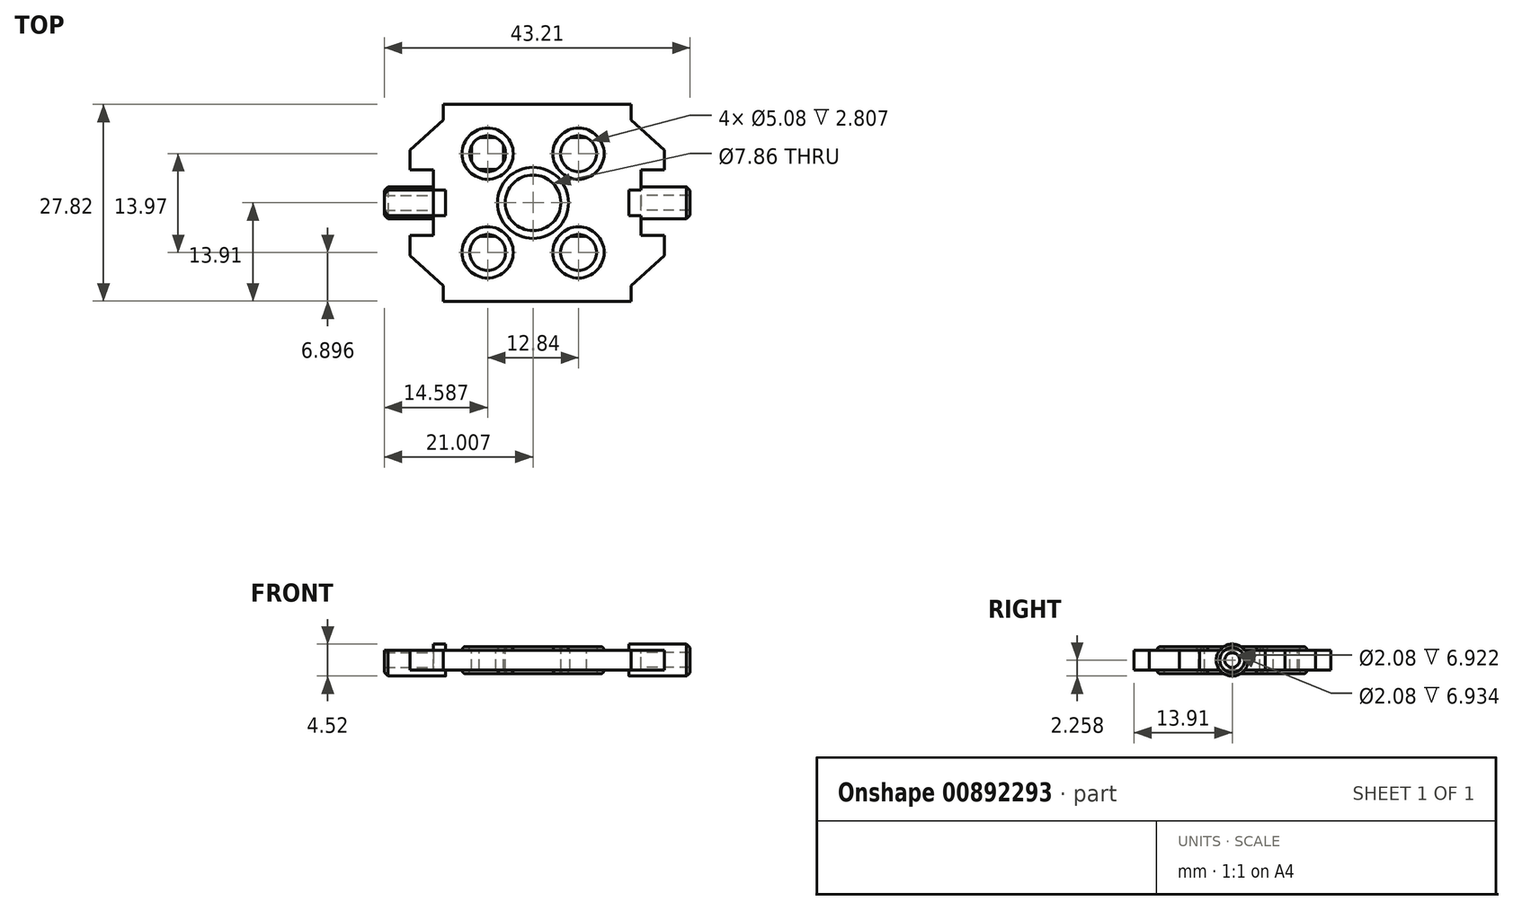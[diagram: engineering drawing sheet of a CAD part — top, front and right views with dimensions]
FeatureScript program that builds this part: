
annotation { "Feature Type Name" : "Feature", "Feature Type Description" : "" }
export const myFeature = defineFeature(function(context is Context, id is Id, definition is map)
    precondition{}
    {
        {
            var Q0;
            Q0=qCreatedBy(makeId("Top.planeOp"),FACE);
            var sketch = newSketch(context, id + "F0", { "sketchPlane" : qUnion([Q0])});
            skLineSegment(sketch, "E0.bottom", {"start": v(-17.98, 13.91) * mm, "end": v(17.98, 13.91) * mm});
            skLineSegment(sketch, "E0.top", {"start": v(-17.98, -13.91) * mm, "end": v(17.98, -13.91) * mm});
            skLineSegment(sketch, "E0.left", {"start": v(-17.98, 13.91) * mm, "end": v(-17.98, -13.91) * mm});
            skLineSegment(sketch, "E0.right", {"start": v(17.98, 13.91) * mm, "end": v(17.98, -13.91) * mm});
            skLineSegment(sketch, "E1", {"start": v(17.98, 0) * mm, "end": v(-17.98, 0) * mm});
            skSolve(sketch);
        }
        {
            var Q0;
            Q0=qSketchRegion(id+"F0",true);
            extrude(context, id + "F1", {"entities" : qUnion([Q0]), "depth" : 2.76 * mm, "offsetDistance" : 25.4 * mm});
        }
        {
            var Q0;
            Q0=makeQuery(id+"F1.opExtrude","CAP_FACE",FACE,{"disambiguationData":[OSD([sQuery(id+"F0.wireOp",EDGE,"E0.bottom"),sQuery(id+"F0.wireOp",EDGE,"E0.top"),sQuery(id+"F0.wireOp",EDGE,"E0.left"),sQuery(id+"F0.wireOp",EDGE,"E0.right")])],"isStart":false});
            var sketch = newSketch(context, id + "F2", { "sketchPlane" : qUnion([Q0])});
            skPoint(sketch, "E2", {"position": v(26.78, 13.91) * mm});
            skLineSegment(sketch, "E3", {"start": v(17.98, 0) * mm, "end": v(17.98, 3.7) * mm});
            skLineSegment(sketch, "E4", {"start": v(17.98, 3.7) * mm, "end": v(17.98, 6.51) * mm});
            skLineSegment(sketch, "E5", {"start": v(17.98, -5.58) * mm, "end": v(17.98, -8.4) * mm});
            skPoint(sketch, "E6", {"position": v(26.78, -13.91) * mm});
            skPoint(sketch, "E7", {"position": v(-13.25, -13.91) * mm});
            skPoint(sketch, "E8", {"position": v(-13.25, 13.91) * mm});
            skLineSegment(sketch, "E9", {"start": v(-14.67, 0) * mm, "end": v(-14.67, 4.64) * mm});
            skLineSegment(sketch, "E10", {"start": v(-14.67, 0) * mm, "end": v(-14.67, -4.64) * mm});
            skLineSegment(sketch, "E11", {"start": v(-14.67, -4.64) * mm, "end": v(-17.98, -4.64) * mm});
            skLineSegment(sketch, "E12", {"start": v(-14.67, 4.64) * mm, "end": v(-17.98, 4.64) * mm});
            skLineSegment(sketch, "E13", {"start": v(-13.25, 13.91) * mm, "end": v(-13.25, 11.74) * mm});
            skLineSegment(sketch, "E14", {"start": v(-13.25, -13.91) * mm, "end": v(-13.25, -11.74) * mm});
            skLineSegment(sketch, "E15", {"start": v(-17.98, -4.64) * mm, "end": v(-17.98, -7.45) * mm});
            skLineSegment(sketch, "E16", {"start": v(-17.98, 4.64) * mm, "end": v(-17.98, 7.45) * mm});
            skLineSegment(sketch, "E17", {"start": v(-17.98, 7.45) * mm, "end": v(-13.25, 11.74) * mm});
            skLineSegment(sketch, "E18", {"start": v(-13.25, -11.74) * mm, "end": v(-17.98, -7.45) * mm});
            skCircle(sketch, "E19", {"center": v(-0.6, 0) * mm, "radius": 3.93 * mm});
            skLineSegment(sketch, "E20", {"start": v(17.98, 6.96) * mm, "end": v(-32.7, 6.96) * mm, "construction": true});
            skLineSegment(sketch, "E21", {"start": v(17.98, 0) * mm, "end": v(17.98, 13.91) * mm, "construction": true});
            skPoint(sketch, "E22", {"position": v(-7.01, 6.96) * mm});
            skPoint(sketch, "E23", {"position": v(5.83, 6.96) * mm});
            skPoint(sketch, "E24", {"position": v(18.67, 6.96) * mm});
            skPoint(sketch, "E25", {"position": v(31.5, 6.96) * mm});
            skPoint(sketch, "E26", {"position": v(-19.85, 6.96) * mm});
            skLineSegment(sketch, "E27", {"start": v(-7.01, 6.96) * mm, "end": v(-7.01, -13.91) * mm, "construction": true});
            skLineSegment(sketch, "E28", {"start": v(5.83, 6.96) * mm, "end": v(5.83, -13.91) * mm, "construction": true});
            skLineSegment(sketch, "E29", {"start": v(17.98, 0) * mm, "end": v(17.98, -13.91) * mm, "construction": true});
            skPoint(sketch, "E30", {"position": v(17.98, -6.96) * mm});
            skLineSegment(sketch, "E31", {"start": v(17.98, -6.96) * mm, "end": v(-17.98, -6.96) * mm, "construction": true});
            skCircle(sketch, "E32", {"center": v(-7.01, 6.96) * mm, "radius": 2.54 * mm});
            skPoint(sketch, "E33", {"position": v(5.83, 0) * mm});
            skPoint(sketch, "E34", {"position": v(18.67, 0) * mm});
            skPoint(sketch, "E35", {"position": v(-7.01, 0) * mm});
            skPoint(sketch, "E36", {"position": v(-19.85, 0) * mm});
            skLineSegment(sketch, "E37", {"start": v(18.67, 0) * mm, "end": v(5.83, 0) * mm});
            skLineSegment(sketch, "E38", {"start": v(-19.85, 0) * mm, "end": v(-7.01, 0) * mm});
            skLineSegment(sketch, "E39.left", {"start": v(16.42, -9.2) * mm, "end": v(16.42, -4.7) * mm});
            skPoint(sketch, "E39.middle", {"position": v(19.26, -6.96) * mm});
            skLineSegment(sketch, "E40.2.1.0", {"start": v(-9.26, 4.7) * mm, "end": v(-4.76, 4.7) * mm});
            skLineSegment(sketch, "E40.2.1.1", {"start": v(-9.26, 4.7) * mm, "end": v(-9.26, 9.2) * mm});
            skLineSegment(sketch, "E40.2.1.2", {"start": v(-9.26, 9.2) * mm, "end": v(-4.76, 9.2) * mm});
            skLineSegment(sketch, "E40.2.1.3", {"start": v(-4.76, 4.7) * mm, "end": v(-4.76, 9.2) * mm});
            skLineSegment(sketch, "E41.bottom", {"start": v(-17.98, 13.91) * mm, "end": v(17.98, 13.91) * mm});
            skLineSegment(sketch, "E41.top", {"start": v(-17.98, -13.91) * mm, "end": v(17.98, -13.91) * mm});
            skLineSegment(sketch, "E41.left", {"start": v(-17.98, 13.91) * mm, "end": v(-17.98, -13.91) * mm});
            skLineSegment(sketch, "E41.right", {"start": v(17.98, 13.91) * mm, "end": v(17.98, -13.91) * mm});
            skPoint(sketch, "E42", {"position": v(0, 13.91) * mm});
            skLineSegment(sketch, "E43", {"start": v(17.98, 13.91) * mm, "end": v(-17.98, 13.91) * mm});
            skLineSegment(sketch, "E44", {"start": v(13.25, 13.91) * mm, "end": v(13.25, 11.74) * mm});
            skLineSegment(sketch, "E45", {"start": v(13.25, 11.74) * mm, "end": v(17.98, 7.45) * mm});
            skLineSegment(sketch, "E46", {"start": v(17.98, 7.45) * mm, "end": v(17.98, 4.64) * mm});
            skLineSegment(sketch, "E47", {"start": v(17.98, 4.64) * mm, "end": v(14.67, 4.64) * mm});
            skLineSegment(sketch, "E48", {"start": v(14.67, 4.64) * mm, "end": v(14.67, -4.64) * mm});
            skLineSegment(sketch, "E49", {"start": v(14.67, -4.64) * mm, "end": v(17.98, -4.64) * mm});
            skLineSegment(sketch, "E50", {"start": v(17.98, -4.64) * mm, "end": v(17.98, -7.45) * mm});
            skLineSegment(sketch, "E51", {"start": v(17.98, -7.45) * mm, "end": v(13.25, -11.74) * mm});
            skLineSegment(sketch, "E52", {"start": v(13.25, -11.74) * mm, "end": v(13.25, -13.91) * mm});
            skPoint(sketch, "E53", {"position": v(14.67, 0) * mm});
            skPoint(sketch, "E54", {"position": v(-4.76, 6.96) * mm});
            skPoint(sketch, "E55", {"position": v(7.94, 6.96) * mm});
            skPoint(sketch, "E55.positionSnap0", {"position": v(8.07, 6.96) * mm});
            skPoint(sketch, "E56", {"position": v(-4.76, -6.96) * mm});
            skPoint(sketch, "E57", {"position": v(8.07, -6.96) * mm});
            skCircle(sketch, "E58.0.1.0", {"center": v(-7.01, -7.01) * mm, "radius": 2.54 * mm});
            skLineSegment(sketch, "E58.0.1.1", {"start": v(-9.26, -4.77) * mm, "end": v(-4.76, -4.77) * mm});
            skLineSegment(sketch, "E58.0.1.2", {"start": v(-4.76, -9.26) * mm, "end": v(-4.76, -4.77) * mm});
            skLineSegment(sketch, "E58.0.1.3", {"start": v(-9.26, -9.26) * mm, "end": v(-4.76, -9.26) * mm});
            skLineSegment(sketch, "E58.0.1.4", {"start": v(-9.26, -9.26) * mm, "end": v(-9.26, -4.77) * mm});
            skCircle(sketch, "E58.1.0.0", {"center": v(5.83, 6.96) * mm, "radius": 2.54 * mm});
            skLineSegment(sketch, "E58.1.0.1", {"start": v(3.58, 9.2) * mm, "end": v(8.07, 9.2) * mm});
            skLineSegment(sketch, "E58.1.0.2", {"start": v(8.07, 4.7) * mm, "end": v(8.07, 9.2) * mm});
            skLineSegment(sketch, "E58.1.0.3", {"start": v(3.58, 4.7) * mm, "end": v(8.07, 4.7) * mm});
            skLineSegment(sketch, "E58.1.0.4", {"start": v(3.58, 4.7) * mm, "end": v(3.58, 9.2) * mm});
            skCircle(sketch, "E58.1.1.0", {"center": v(5.83, -7.01) * mm, "radius": 2.54 * mm});
            skLineSegment(sketch, "E58.1.1.1", {"start": v(3.58, -4.77) * mm, "end": v(8.07, -4.77) * mm});
            skLineSegment(sketch, "E58.1.1.2", {"start": v(8.07, -9.26) * mm, "end": v(8.07, -4.77) * mm});
            skLineSegment(sketch, "E58.1.1.3", {"start": v(3.58, -9.26) * mm, "end": v(8.07, -9.26) * mm});
            skLineSegment(sketch, "E58.1.1.4", {"start": v(3.58, -9.26) * mm, "end": v(3.58, -4.77) * mm});
            skLineSegment(sketch, "E58.direction1", {"start": v(-7.01, 6.96) * mm, "end": v(5.83, 6.96) * mm, "construction": true});
            skLineSegment(sketch, "E58.direction2", {"start": v(-7.01, 6.96) * mm, "end": v(-7.01, -7.01) * mm, "construction": true});
            skLineSegment(sketch, "E59", {"start": v(5.83, 0) * mm, "end": v(-0.6, 0) * mm});
            skLineSegment(sketch, "E60", {"start": v(-7.01, 0) * mm, "end": v(-0.6, 0) * mm});
            skSolve(sketch);
        }
        {
            var Q0;
            Q0=makeQuery(id+"F2.imprint","IMPRINT",FACE,{"disambiguationData":[TD([[makeQuery(id+"F2.imprint","IMPRINT",EDGE,{"derivedFrom":sQuery(id+"F2.wireOp",EDGE,"zKyvtmt8-tCjY-tQvq-sh6t-lBbuTK4CHgfQ")}),1.0]])]});
            var Q1;
            {var subQ0=sQuery(id+"F2.wireOp",EDGE,"nGXZYah3-xuGq-2yHy-m2No-0d3Pi9Qq722P");Q1=makeQuery(id+"F2.imprint","IMPRINT",FACE,{"disambiguationData":[TD([[makeQuery(id+"F2.imprint","IMPRINT",EDGE,{"derivedFrom":subQ0}),1.0]])]});}
            var Q2;
            {var subQ0=sQuery(id+"F2.wireOp",EDGE,"yPbE09O0-nCyG-tVRH-j9K3-g5R8uc3CmmFN");Q2=makeQuery(id+"F2.imprint","IMPRINT",FACE,{"disambiguationData":[TD([[makeQuery(id+"F2.imprint","IMPRINT",EDGE,{"derivedFrom":subQ0}),-1.0]])]});}
            var Q3;
            {var subQ0=sQuery(id+"F2.wireOp",EDGE,"E14");Q3=makeQuery(id+"F2.imprint","IMPRINT",FACE,{"disambiguationData":[TD([[makeQuery(id+"F2.imprint","IMPRINT",EDGE,{"derivedFrom":subQ0}),1.0]])]});}
            var Q4;
            Q4=makeQuery(id+"F2.imprint","IMPRINT",FACE,{"disambiguationData":[TD([[makeQuery(id+"F2.imprint","IMPRINT",EDGE,{"derivedFrom":sQuery(id+"F2.wireOp",EDGE,"E9")}),1.0]])]});
            var Q5;
            {var subQ0=sQuery(id+"F2.wireOp",EDGE,"E13");Q5=makeQuery(id+"F2.imprint","IMPRINT",FACE,{"disambiguationData":[TD([[makeQuery(id+"F2.imprint","IMPRINT",EDGE,{"derivedFrom":subQ0}),-1.0]])]});}
            extrude(context, id + "F3", {"entities" : qUnion([Q0, Q1, Q2, Q3, Q4, Q5]), "operationType" : NewBodyOperationType.REMOVE, "oppositeDirection" : true, "depth" : 25.4 * mm, "offsetDistance" : 25.4 * mm});
        }
        {
            var Q0;
            Q0=makeQuery(id+"F2.imprint","IMPRINT",FACE,{"disambiguationData":[TD([[makeQuery(id+"F2.imprint","IMPRINT",EDGE,{"derivedFrom":sQuery(id+"F2.wireOp",EDGE,"fuK7n6Y2-Enzt-2XlE-SA73-k2Jc5K4om95h")}),1.0]])]});
            var Q1;
            {var subQ0=sQuery(id+"F2.wireOp",EDGE,"sv07lWKE-gPZX-1UWt-FJWq-DTTsMFg5NSMi");var subQ1=sQuery(id+"F2.wireOp",EDGE,"E38");var subQ2=makeQuery(id+"F2.imprint","INTERSECT",VERTEX,{"disambiguationData":[OD(0.0)],"derivedFrom":[subQ1,subQ0]});Q1=makeQuery(id+"F2.imprint","IMPRINT",FACE,{"disambiguationData":[TD([[makeQuery(id+"F2.imprint","IMPRINT",EDGE,{"disambiguationData":[TD([[subQ2,-1.0]])],"derivedFrom":subQ1}),-1.0]])]});}
            var Q2;
            {var subQ0=sQuery(id+"F2.wireOp",EDGE,"sv07lWKE-gPZX-1UWt-FJWq-DTTsMFg5NSMi");var subQ1=sQuery(id+"F2.wireOp",EDGE,"E38");var subQ2=makeQuery(id+"F2.imprint","INTERSECT",VERTEX,{"disambiguationData":[OD(0.0)],"derivedFrom":[subQ1,subQ0]});Q2=makeQuery(id+"F2.imprint","IMPRINT",FACE,{"disambiguationData":[TD([[makeQuery(id+"F2.imprint","IMPRINT",EDGE,{"disambiguationData":[TD([[subQ2,-1.0]])],"derivedFrom":subQ1}),1.0]])]});}
            var Q3;
            Q3=makeQuery(id+"F2.imprint","IMPRINT",FACE,{"disambiguationData":[TD([[makeQuery(id+"F2.imprint","IMPRINT",EDGE,{"derivedFrom":sQuery(id+"F2.wireOp",EDGE,"E19")}),1.0]])]});
            var Q4;
            {var subQ0=sQuery(id+"F2.wireOp",EDGE,"gV5skUVd-Vbjl-6Grx-gXeV-zpvUfDL4PLVQ");var subQ1=sQuery(id+"F2.wireOp",EDGE,"E37");var subQ2=makeQuery(id+"F2.imprint","INTERSECT",VERTEX,{"disambiguationData":[OD(0.0)],"derivedFrom":[subQ1,subQ0]});Q4=makeQuery(id+"F2.imprint","IMPRINT",FACE,{"disambiguationData":[TD([[makeQuery(id+"F2.imprint","IMPRINT",EDGE,{"disambiguationData":[TD([[subQ2,1.0]])],"derivedFrom":subQ1}),1.0]])]});}
            var Q5;
            {var subQ0=sQuery(id+"F2.wireOp",EDGE,"gV5skUVd-Vbjl-6Grx-gXeV-zpvUfDL4PLVQ");var subQ1=sQuery(id+"F2.wireOp",EDGE,"E37");var subQ2=makeQuery(id+"F2.imprint","INTERSECT",VERTEX,{"disambiguationData":[OD(0.0)],"derivedFrom":[subQ1,subQ0]});Q5=makeQuery(id+"F2.imprint","IMPRINT",FACE,{"disambiguationData":[TD([[makeQuery(id+"F2.imprint","IMPRINT",EDGE,{"disambiguationData":[TD([[subQ2,1.0]])],"derivedFrom":subQ1}),-1.0]])]});}
            var Q6;
            Q6=makeQuery(id+"F2.imprint","IMPRINT",FACE,{"disambiguationData":[TD([[makeQuery(id+"F2.imprint","IMPRINT",EDGE,{"derivedFrom":sQuery(id+"F2.wireOp",EDGE,"omkNjfGR-ckuW-d5aa-qWtX-TfsBPBlHMN8u")}),1.0]])]});
            var Q7;
            Q7=makeQuery(id+"F2.imprint","IMPRINT",FACE,{"disambiguationData":[TD([[makeQuery(id+"F2.imprint","IMPRINT",EDGE,{"derivedFrom":sQuery(id+"F2.wireOp",EDGE,"E32")}),1.0]])]});
            var Q8;
            Q8=makeQuery(id+"F2.imprint","IMPRINT",FACE,{"disambiguationData":[TD([[makeQuery(id+"F2.imprint","IMPRINT",EDGE,{"derivedFrom":sQuery(id+"F2.wireOp",EDGE,"wbXKtzry-o3Vx-0E5J-MFbw-KvrlOybN9rRN")}),1.0]])]});
            var Q9;
            Q9=makeQuery(id+"F2.imprint","IMPRINT",FACE,{"disambiguationData":[TD([[makeQuery(id+"F2.imprint","IMPRINT",EDGE,{"derivedFrom":sQuery(id+"F2.wireOp",EDGE,"Ppe3M46U-QorI-ucGU-aqDp-dvkcDBRh25Wz")}),1.0]])]});
            var Q10;
            Q10=makeQuery(id+"F2.imprint","IMPRINT",FACE,{"disambiguationData":[TD([[makeQuery(id+"F2.imprint","IMPRINT",EDGE,{"derivedFrom":sQuery(id+"F2.wireOp",EDGE,"4vAETKog-jQpa-BSM7-OqoW-5IxsvznHgaLA")}),1.0]])]});
            var Q11;
            Q11=makeQuery(id+"F2.imprint","IMPRINT",FACE,{"disambiguationData":[TD([[makeQuery(id+"F2.imprint","IMPRINT",EDGE,{"derivedFrom":sQuery(id+"F2.wireOp",EDGE,"5XKSeXba-nxxC-YXAP-KxCt-XMvB8Zbv8VPG")}),1.0]])]});
            var Q12;
            Q12=makeQuery(id+"F2.imprint","IMPRINT",FACE,{"disambiguationData":[TD([[makeQuery(id+"F2.imprint","IMPRINT",EDGE,{"derivedFrom":sQuery(id+"F2.wireOp",EDGE,"9KXrDHUh-3l1R-qzUI-8NNp-dQZea570rMoK")}),1.0]])]});
            var Q13;
            {var subQ4=sQuery(id+"F2.wireOp",EDGE,"E44");Q13=makeQuery(id+"F2.imprint","IMPRINT",FACE,{"disambiguationData":[TD([[makeQuery(id+"F2.imprint","IMPRINT",EDGE,{"derivedFrom":subQ4}),1.0]])]});}
            var Q14;
            {var subQ0=sQuery(id+"F2.wireOp",EDGE,"E52");Q14=makeQuery(id+"F2.imprint","IMPRINT",FACE,{"disambiguationData":[TD([[makeQuery(id+"F2.imprint","IMPRINT",EDGE,{"derivedFrom":subQ0}),1.0]])]});}
            var Q15;
            {var subQ1=sQuery(id+"F2.wireOp",EDGE,"E58.1.0.0");var subQ8=sQuery(id+"F2.wireOp",EDGE,"E58.1.0.1");var subQ11=makeQuery(id+"F2.imprint","INTERSECT",VERTEX,{"disambiguationData":[OD(0.0)],"derivedFrom":[subQ1,subQ8]});Q15=makeQuery(id+"F2.imprint","IMPRINT",FACE,{"disambiguationData":[TD([[makeQuery(id+"F2.imprint","IMPRINT",EDGE,{"disambiguationData":[TD([[subQ11,1.0]])],"derivedFrom":subQ1}),1.0]])]});}
            var Q16;
            {var subQ1=sQuery(id+"F2.wireOp",EDGE,"E58.1.1.0");var subQ8=sQuery(id+"F2.wireOp",EDGE,"E58.1.1.1");var subQ11=makeQuery(id+"F2.imprint","INTERSECT",VERTEX,{"disambiguationData":[OD(0.0)],"derivedFrom":[subQ1,subQ8]});Q16=makeQuery(id+"F2.imprint","IMPRINT",FACE,{"disambiguationData":[TD([[makeQuery(id+"F2.imprint","IMPRINT",EDGE,{"disambiguationData":[TD([[subQ11,1.0]])],"derivedFrom":subQ1}),1.0]])]});}
            var Q17;
            {var subQ1=sQuery(id+"F2.wireOp",EDGE,"E58.0.1.0");var subQ8=sQuery(id+"F2.wireOp",EDGE,"E58.0.1.1");var subQ11=makeQuery(id+"F2.imprint","INTERSECT",VERTEX,{"disambiguationData":[OD(0.0)],"derivedFrom":[subQ1,subQ8]});Q17=makeQuery(id+"F2.imprint","IMPRINT",FACE,{"disambiguationData":[TD([[makeQuery(id+"F2.imprint","IMPRINT",EDGE,{"disambiguationData":[TD([[subQ11,1.0]])],"derivedFrom":subQ1}),1.0]])]});}
            extrude(context, id + "F4", {"entities" : qUnion([Q0, Q1, Q2, Q3, Q4, Q5, Q6, Q7, Q8, Q9, Q10, Q11, Q12, Q13, Q14, Q15, Q16, Q17]), "operationType" : NewBodyOperationType.REMOVE, "oppositeDirection" : true, "depth" : 25.4 * mm, "offsetDistance" : 25.4 * mm});
        }
        {
            var Q0;
            Q0=makeQuery(id+"F3.boolean.opBoolean","COPY",FACE,{"derivedFrom":makeQuery(id+"F3.opExtrude","SWEPT_FACE",FACE,{"disambiguationData":[OSD([sQuery(id+"F2.wireOp",EDGE,"E9"),sQuery(id+"F2.wireOp",EDGE,"E10")])]})});
            var sketch = newSketch(context, id + "F5", { "sketchPlane" : qUnion([Q0])});
            skLineSegment(sketch, "E61", {"start": v(0, 0) * mm, "end": v(0, 2.76) * mm, "construction": true});
            skCircle(sketch, "E62", {"center": v(0, 1.38) * mm, "radius": 2.26 * mm});
            skCircle(sketch, "E63", {"center": v(0, 1.38) * mm, "radius": 1.04 * mm});
            skSolve(sketch);
        }
        {
            var Q0;
            Q0=makeQuery(id+"F5.imprint","IMPRINT",FACE,{"disambiguationData":[TD([[makeQuery(id+"F5.imprint","IMPRINT",EDGE,{"derivedFrom":sQuery(id+"F5.wireOp",EDGE,"E63")}),-1.0]])]});
            var Q1;
            {var subQ0=sQuery(id+"F5.wireOp",EDGE,"E62");var subQ1=makeQuery(id+"F3.boolean.opBoolean","COPY",EDGE,{"derivedFrom":makeQuery(id+"F3.opExtrude","CAP_EDGE",EDGE,{"disambiguationData":[OSD([sQuery(id+"F2.wireOp",EDGE,"E9"),sQuery(id+"F2.wireOp",EDGE,"E10")])],"isStart":true})});var subQ2=makeQuery(id+"F5.imprint","INTERSECT",VERTEX,{"disambiguationData":[OD(0.0)],"derivedFrom":[subQ1,subQ0]});Q1=makeQuery(id+"F5.imprint","IMPRINT",FACE,{"disambiguationData":[TD([[makeQuery(id+"F5.imprint","IMPRINT",EDGE,{"disambiguationData":[TD([[subQ2,1.0]])],"derivedFrom":subQ0}),1.0]])]});}
            var Q2;
            {var subQ0=sQuery(id+"F5.wireOp",EDGE,"E62");var subQ1=makeQuery(id+"F3.boolean.opBoolean","INTERSECT",EDGE,{"derivedFrom":[makeQuery(id+"F1.opExtrude","CAP_FACE",FACE,{"disambiguationData":[OSD([sQuery(id+"F0.wireOp",EDGE,"E0.bottom"),sQuery(id+"F0.wireOp",EDGE,"E0.top"),sQuery(id+"F0.wireOp",EDGE,"E0.left"),sQuery(id+"F0.wireOp",EDGE,"E0.right")])],"isStart":true}),makeQuery(id+"F3.opExtrude","SWEPT_FACE",FACE,{"disambiguationData":[OSD([sQuery(id+"F2.wireOp",EDGE,"E9"),sQuery(id+"F2.wireOp",EDGE,"E10")])]})]});var subQ2=makeQuery(id+"F5.imprint","INTERSECT",VERTEX,{"disambiguationData":[OD(0.0)],"derivedFrom":[subQ1,subQ0]});Q2=makeQuery(id+"F5.imprint","IMPRINT",FACE,{"disambiguationData":[TD([[makeQuery(id+"F5.imprint","IMPRINT",EDGE,{"disambiguationData":[TD([[subQ2,-1.0]])],"derivedFrom":subQ0}),1.0]])]});}
            var Q3;
            {var subQ0=sQuery(id+"F5.wireOp",EDGE,"E62");var subQ1=makeQuery(id+"F4.boolean.opBoolean","INTERSECT",EDGE,{"derivedFrom":[makeQuery(id+"F1.opExtrude","CAP_FACE",FACE,{"disambiguationData":[OSD([sQuery(id+"F0.wireOp",EDGE,"E0.bottom"),sQuery(id+"F0.wireOp",EDGE,"E0.top"),sQuery(id+"F0.wireOp",EDGE,"E0.left"),sQuery(id+"F0.wireOp",EDGE,"E0.right")])],"isStart":true}),makeQuery(id+"F4.opExtrude","SWEPT_FACE",FACE,{"disambiguationData":[OSD([sQuery(id+"F2.wireOp",EDGE,"E9"),sQuery(id+"F2.wireOp",EDGE,"E10")])]})]});var subQ2=makeQuery(id+"F5.imprint","INTERSECT",VERTEX,{"disambiguationData":[OD(0.0)],"derivedFrom":[subQ1,subQ0]});Q3=makeQuery(id+"F5.imprint","IMPRINT",FACE,{"disambiguationData":[TD([[makeQuery(id+"F5.imprint","IMPRINT",EDGE,{"disambiguationData":[TD([[subQ2,-1.0]])],"derivedFrom":subQ0}),1.0]])]});}
            extrude(context, id + "F6", {"entities" : qUnion([Q0, Q1, Q2, Q3]), "operationType" : NewBodyOperationType.ADD, "depth" : 6.92 * mm, "offsetDistance" : 25.4 * mm});
        }
        {
            var Q0;
            {var subQ0=sQuery(id+"F5.wireOp",EDGE,"E62");Q0=makeQuery(id+"F6.boolean.opBoolean","SPLIT",FACE,{"disambiguationData":[TD([makeQuery(id+"F1.opExtrude","CAP_FACE",FACE,{"disambiguationData":[OSD([sQuery(id+"F0.wireOp",EDGE,"E0.bottom"),sQuery(id+"F0.wireOp",EDGE,"E0.top"),sQuery(id+"F0.wireOp",EDGE,"E0.left"),sQuery(id+"F0.wireOp",EDGE,"E0.right")])],"isStart":false})])],"derivedFrom":makeQuery(id+"F6.opExtrude","CAP_FACE",FACE,{"disambiguationData":[OSD([subQ0,sQuery(id+"F5.wireOp",EDGE,"E63")])],"isStart":true})});}
            var sketch = newSketch(context, id + "F7", { "sketchPlane" : qUnion([Q0])});
            skCircle(sketch, "E64.0.0", {"center": v(0, 1.38) * mm, "radius": 2.26 * mm});
            skSolve(sketch);
        }
        {
            var Q0;
            Q0=qSketchRegion(id+"F7",true);
            extrude(context, id + "F8", {"entities" : qUnion([Q0]), "operationType" : NewBodyOperationType.ADD, "depth" : 1.71 * mm, "offsetDistance" : 25.4 * mm});
        }
        {
            var Q0;
            Q0=makeQuery(id+"F1.opExtrude","CAP_FACE",FACE,{"disambiguationData":[OSD([sQuery(id+"F0.wireOp",EDGE,"E0.bottom"),sQuery(id+"F0.wireOp",EDGE,"E0.top"),sQuery(id+"F0.wireOp",EDGE,"E0.left"),sQuery(id+"F0.wireOp",EDGE,"E0.right")])],"isStart":false});
            var sketch = newSketch(context, id + "F9", { "sketchPlane" : qUnion([Q0])});
            skCircle(sketch, "E65.1.0.0", {"center": v(-7.01, 6.96) * mm, "radius": 2.54 * mm});
            skCircle(sketch, "E65.1.0.1", {"center": v(-7.01, 6.96) * mm, "radius": 3.62 * mm});
            skCircle(sketch, "E65.1.1.0", {"center": v(-7.01, -7.01) * mm, "radius": 2.54 * mm});
            skCircle(sketch, "E65.1.1.1", {"center": v(-7.01, -7.01) * mm, "radius": 3.62 * mm});
            skCircle(sketch, "E65.2.0.0", {"center": v(5.83, 6.96) * mm, "radius": 2.54 * mm});
            skCircle(sketch, "E65.2.0.1", {"center": v(5.83, 6.96) * mm, "radius": 3.62 * mm});
            skCircle(sketch, "E65.2.1.0", {"center": v(5.83, -7.01) * mm, "radius": 2.54 * mm});
            skCircle(sketch, "E65.2.1.1", {"center": v(5.83, -7.01) * mm, "radius": 3.62 * mm});
            skLineSegment(sketch, "E65.direction1", {"start": v(-19.85, 6.96) * mm, "end": v(-7.01, 6.96) * mm, "construction": true});
            skLineSegment(sketch, "E65.direction2", {"start": v(-19.85, 6.96) * mm, "end": v(-19.85, -7.01) * mm, "construction": true});
            skCircle(sketch, "E66", {"center": v(-0.6, 0) * mm, "radius": 5.02 * mm});
            skCircle(sketch, "E67.1", {"center": v(-0.6, 0) * mm, "radius": 3.93 * mm});
            skSolve(sketch);
        }
        {
            var Q0;
            Q0=qSketchRegion(id+"F9",true);
            extrude(context, id + "F10", {"entities" : qUnion([Q0]), "operationType" : NewBodyOperationType.ADD, "depth" : 0.53 * mm, "offsetDistance" : 25.4 * mm});
        }
        {
            var Q0;
            Q0=makeQuery(id+"F1.opExtrude","CAP_FACE",FACE,{"disambiguationData":[OSD([sQuery(id+"F0.wireOp",EDGE,"E0.bottom"),sQuery(id+"F0.wireOp",EDGE,"E0.top"),sQuery(id+"F0.wireOp",EDGE,"E0.left"),sQuery(id+"F0.wireOp",EDGE,"E0.right")])],"isStart":true});
            var sketch = newSketch(context, id + "F11", { "sketchPlane" : qUnion([Q0])});
            skCircle(sketch, "E68.1.0.0", {"center": v(-7.01, -6.96) * mm, "radius": 3.62 * mm});
            skCircle(sketch, "E68.1.0.1", {"center": v(-7.01, -6.96) * mm, "radius": 2.54 * mm});
            skCircle(sketch, "E68.1.1.0", {"center": v(-7.01, 7.01) * mm, "radius": 3.62 * mm});
            skCircle(sketch, "E68.1.1.1", {"center": v(-7.01, 7.01) * mm, "radius": 2.54 * mm});
            skCircle(sketch, "E68.2.0.0", {"center": v(5.83, -6.96) * mm, "radius": 3.62 * mm});
            skCircle(sketch, "E68.2.0.1", {"center": v(5.83, -6.96) * mm, "radius": 2.54 * mm});
            skCircle(sketch, "E68.2.1.0", {"center": v(5.83, 7.01) * mm, "radius": 3.62 * mm});
            skCircle(sketch, "E68.2.1.1", {"center": v(5.83, 7.01) * mm, "radius": 2.54 * mm});
            skLineSegment(sketch, "E68.direction1", {"start": v(-19.85, -6.96) * mm, "end": v(-7.01, -6.96) * mm, "construction": true});
            skLineSegment(sketch, "E68.direction2", {"start": v(-19.85, -6.96) * mm, "end": v(-19.85, 7.01) * mm, "construction": true});
            skCircle(sketch, "E69.2", {"center": v(-0.6, 0) * mm, "radius": 3.93 * mm});
            skCircle(sketch, "E69.3", {"center": v(-0.6, 0) * mm, "radius": 5.02 * mm});
            skSolve(sketch);
        }
        {
            var Q0;
            Q0=qSketchRegion(id+"F11",true);
            extrude(context, id + "F12", {"entities" : qUnion([Q0]), "operationType" : NewBodyOperationType.ADD, "depth" : 0.53 * mm, "offsetDistance" : 25.4 * mm});
        }
        {
            var Q0;
            Q0=makeQuery(id+"F4.boolean.opBoolean","COPY",FACE,{"derivedFrom":makeQuery(id+"F4.opExtrude","SWEPT_FACE",FACE,{"disambiguationData":[OSD([sQuery(id+"F2.wireOp",EDGE,"E48")])]})});
            var sketch = newSketch(context, id + "F13", { "sketchPlane" : qUnion([Q0])});
            skCircle(sketch, "E70.1", {"center": v(0, 1.38) * mm, "radius": 1.04 * mm});
            skCircle(sketch, "E71.0", {"center": v(0, 1.38) * mm, "radius": 2.26 * mm});
            skSolve(sketch);
        }
        {
            var Q0;
            Q0 = qSketchRegion(id + "F13", true);
            extrude(context, id + "F14", {"entities" : qUnion([Q0]), "operationType" : NewBodyOperationType.ADD, "depth" : 6.93 * mm, "offsetDistance" : 25.4 * mm});
        }
        {
            var Q0;
            {var subQ0=sQuery(id+"F13.wireOp",EDGE,"E70.0");Q0=makeQuery(id+"F14.boolean.opBoolean","SPLIT",FACE,{"disambiguationData":[TD([makeQuery(id+"F1.opExtrude","CAP_FACE",FACE,{"disambiguationData":[OSD([sQuery(id+"F0.wireOp",EDGE,"E0.bottom"),sQuery(id+"F0.wireOp",EDGE,"E0.top"),sQuery(id+"F0.wireOp",EDGE,"E0.left"),sQuery(id+"F0.wireOp",EDGE,"E0.right")])],"isStart":true})])],"derivedFrom":makeQuery(id+"F14.opExtrude","CAP_FACE",FACE,{"disambiguationData":[OSD([subQ0,sQuery(id+"F13.wireOp",EDGE,"E70.1")])],"isStart":true})});}
            var sketch = newSketch(context, id + "F15", { "sketchPlane" : qUnion([Q0])});
            skCircle(sketch, "E72.1", {"center": v(0, 1.38) * mm, "radius": 1.04 * mm});
            skCircle(sketch, "E73.0", {"center": v(0, 1.38) * mm, "radius": 2.26 * mm});
            skSolve(sketch);
        }
        {
            var Q0;
            Q0 = qSketchRegion(id + "F15", true);
            extrude(context, id + "F16", {"entities" : qUnion([Q0]), "operationType" : NewBodyOperationType.ADD, "depth" : 1.73 * mm, "offsetDistance" : 25.4 * mm});
        }
        {
            var Q0;
            Q0=makeQuery(id+"F14.opExtrude","CAP_EDGE",EDGE,{"disambiguationData":[OSD([sQuery(id+"F13.wireOp",EDGE,"E71.0")])],"isStart":false});
            var Q1;
            Q1=makeQuery(id+"F6.opExtrude","CAP_EDGE",EDGE,{"disambiguationData":[OSD([sQuery(id+"F5.wireOp",EDGE,"E62")])],"isStart":false});
            chamfer(context, id + "F17", {"entities" : qUnion([Q0, Q1]), "width" : 0.5 * mm, "tangentPropagation" : true});
        }
        {
            var Q0;
            Q0=makeQuery(id+"F12.opExtrude","CAP_EDGE",EDGE,{"disambiguationData":[OSD([sQuery(id+"F11.wireOp",EDGE,"E69.3")])],"isStart":false});
            var Q1;
            Q1=makeQuery(id+"F12.opExtrude","CAP_EDGE",EDGE,{"disambiguationData":[OSD([sQuery(id+"F11.wireOp",EDGE,"E68.2.1.0")])],"isStart":false});
            var Q2;
            Q2=makeQuery(id+"F12.opExtrude","CAP_EDGE",EDGE,{"disambiguationData":[OSD([sQuery(id+"F11.wireOp",EDGE,"E68.1.1.0")])],"isStart":false});
            var Q3;
            Q3=makeQuery(id+"F12.opExtrude","CAP_EDGE",EDGE,{"disambiguationData":[OSD([sQuery(id+"F11.wireOp",EDGE,"E68.1.0.0")])],"isStart":false});
            var Q4;
            Q4=makeQuery(id+"F10.opExtrude","CAP_EDGE",EDGE,{"disambiguationData":[OSD([sQuery(id+"F9.wireOp",EDGE,"E65.1.0.1")])],"isStart":false});
            var Q5;
            Q5=makeQuery(id+"F10.opExtrude","CAP_EDGE",EDGE,{"disambiguationData":[OSD([sQuery(id+"F9.wireOp",EDGE,"E65.2.0.1")])],"isStart":false});
            var Q6;
            Q6=makeQuery(id+"F10.opExtrude","CAP_EDGE",EDGE,{"disambiguationData":[OSD([sQuery(id+"F9.wireOp",EDGE,"E66")])],"isStart":false});
            var Q7;
            Q7=makeQuery(id+"F10.opExtrude","CAP_EDGE",EDGE,{"disambiguationData":[OSD([sQuery(id+"F9.wireOp",EDGE,"E65.1.1.1")])],"isStart":false});
            var Q8;
            Q8=makeQuery(id+"F10.opExtrude","CAP_EDGE",EDGE,{"disambiguationData":[OSD([sQuery(id+"F9.wireOp",EDGE,"E65.2.1.1")])],"isStart":false});
            var Q9;
            Q9=makeQuery(id+"F10.opExtrude","CAP_EDGE",EDGE,{"disambiguationData":[OSD([sQuery(id+"F9.wireOp",EDGE,"E65.2.1.0")])],"isStart":false});
            var Q10;
            Q10=makeQuery(id+"F10.opExtrude","CAP_EDGE",EDGE,{"disambiguationData":[OSD([sQuery(id+"F9.wireOp",EDGE,"E65.1.1.0")])],"isStart":false});
            var Q11;
            Q11=makeQuery(id+"F10.opExtrude","CAP_EDGE",EDGE,{"disambiguationData":[OSD([sQuery(id+"F9.wireOp",EDGE,"E65.2.0.0")])],"isStart":false});
            var Q12;
            Q12=makeQuery(id+"F10.opExtrude","CAP_EDGE",EDGE,{"disambiguationData":[OSD([sQuery(id+"F9.wireOp",EDGE,"E65.1.0.0")])],"isStart":false});
            var Q13;
            Q13=makeQuery(id+"F12.opExtrude","CAP_EDGE",EDGE,{"disambiguationData":[OSD([sQuery(id+"F11.wireOp",EDGE,"E68.2.1.1")])],"isStart":false});
            var Q14;
            Q14=makeQuery(id+"F12.opExtrude","CAP_EDGE",EDGE,{"disambiguationData":[OSD([sQuery(id+"F11.wireOp",EDGE,"E68.2.0.0")])],"isStart":false});
            var Q15;
            Q15=makeQuery(id+"F12.opExtrude","CAP_EDGE",EDGE,{"disambiguationData":[OSD([sQuery(id+"F11.wireOp",EDGE,"E68.2.0.1")])],"isStart":false});
            var Q16;
            Q16=makeQuery(id+"F12.opExtrude","CAP_EDGE",EDGE,{"disambiguationData":[OSD([sQuery(id+"F11.wireOp",EDGE,"E68.1.0.1")])],"isStart":false});
            var Q17;
            Q17=makeQuery(id+"F12.opExtrude","CAP_EDGE",EDGE,{"disambiguationData":[OSD([sQuery(id+"F11.wireOp",EDGE,"E68.1.1.1")])],"isStart":false});
            var Q18;
            Q18=makeQuery(id+"F12.opExtrude","CAP_EDGE",EDGE,{"disambiguationData":[OSD([sQuery(id+"F11.wireOp",EDGE,"E69.2")])],"isStart":false});
            var Q19;
            Q19=makeQuery(id+"F10.opExtrude","CAP_EDGE",EDGE,{"disambiguationData":[OSD([sQuery(id+"F9.wireOp",EDGE,"E67.1")])],"isStart":false});
            fillet(context, id + "F18", {"entities" : qUnion([Q0, Q1, Q2, Q3, Q4, Q5, Q6, Q7, Q8, Q9, Q10, Q11, Q12, Q13, Q14, Q15, Q16, Q17, Q18, Q19]), "radius" : 0.5 * mm, "tangentPropagation" : true, "allowEdgeOverflow" : false});
        }
    });
